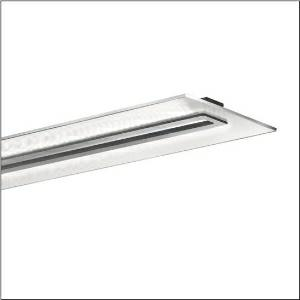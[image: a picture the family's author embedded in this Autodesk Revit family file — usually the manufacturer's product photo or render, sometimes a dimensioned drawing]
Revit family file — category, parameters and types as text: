
# Revit family: vega_11_5mn238dlc003
name_source: partatom
category: Lighting Fixtures
units: mm (PartAtom-declared; Revit-internal decimal feet)

## family parameters
Cut with Voids When Loaded = No
Host = Face
Light Source = No
Part Type = Normal
Room Calculation Point = No
Round Connector Dimension = Use Diameter
Shared = No

## types (1)
- --- (1 x LED 3000K / CRI = 80 (unbekannt), 4300 lm, 3000K)
    Apparent Load = 35 VA
    CIE Flux Codes = 61 86 97 62 100
    Color Rendering = 80
    Color Temperature = 3000K
    Default Elevation = 1800 mm
    Description = Vega 11, office luminaire, primary light control with prismatic reflector, of PMMA, transparent prismatic structure, CAT 2 (L<= 1500cd/m²), light emission: direct/indirect distribution, primary light characteristic: symmetric, installation type: suspended mounting, surface-mounted, LED, rated luminous flux: 4.300lm, luminous efficacy: 123lm/W, light colour: 830, colour temperature: 3000K, control gear: DALI, with terminal, 3+2-pole, max. 2.5mm², mains connection: 230V, AC, 50Hz, connection cable inclusive, cable length: 1,5m, rated input power: 35W, luminaire housing, rectangular, rounded, of aluminium section, anodised, metallic grey (RAL 9006), length: 1.250mm, width: 350mm, height: 43mm, luminaire housing, lower part, of aluminium section, anodised, metallic grey (RAL 9006), of PC, grey, protection rating (complete): IP20, insulation class (complete): insulation class I (protective earthing), certification: CE, standard: EN 50419, packaging unit: 1 piece
    Height = 40 mm  [stored 0.131234 ft]
    Lamp = 1 x LED 3000K / CRI >= 80 (unbekannt)
    Lamp Light Flux = 4300 lm
    Lamp count = 1
    Length = 1250 mm
    Luminous efficacy = 123 lm/W
    Manufacturer = Siteco
    ModVariant = No
    Model = 5MN238DLC003
    Mounting Place = Ceiling
    Mounting Type = Pendant
    Number of Poles = 1
    OnlyDefault = Yes
    Power Factor = 1
    Product Name = Vega 11
    Product group = office luminaire | ceiling pendant
    ProductGroupID = 903
    Protection Class = Protection class I
    Protection Degree = IP 20
    RLX_Detail_Level = 1
    RLX_Emergency_Light_Flux = 0 lm
    RLX_Emergency_Type = 0
    RLX_Emergency_Type_DB = No
    RlxData = <blob elided: 62549 chars, md5=f4ce3c9f>
    Socket = socket
    Standby Power = 0 W
    System Light Flux = 4300 lm
    System Power = 35 W
    Type Comments = factory setting: luminous flux: 100 % | dim-lin: 254 | 260 mA
    Type Image = l_1004807.jpg
    URL = http://relux.com
    VarID = @adj_197063
    Voltage = 0 V
    Weight = 0.00 kg
    Width = 350 mm

note: [stored X ft] marks values corroborated as IEEE doubles in the binary element streams (Revit-internal decimal feet)

## geometry (parser evidence)
native form markers: Blend x4, Sweep x13
no freeform markers — native parametric forms only
